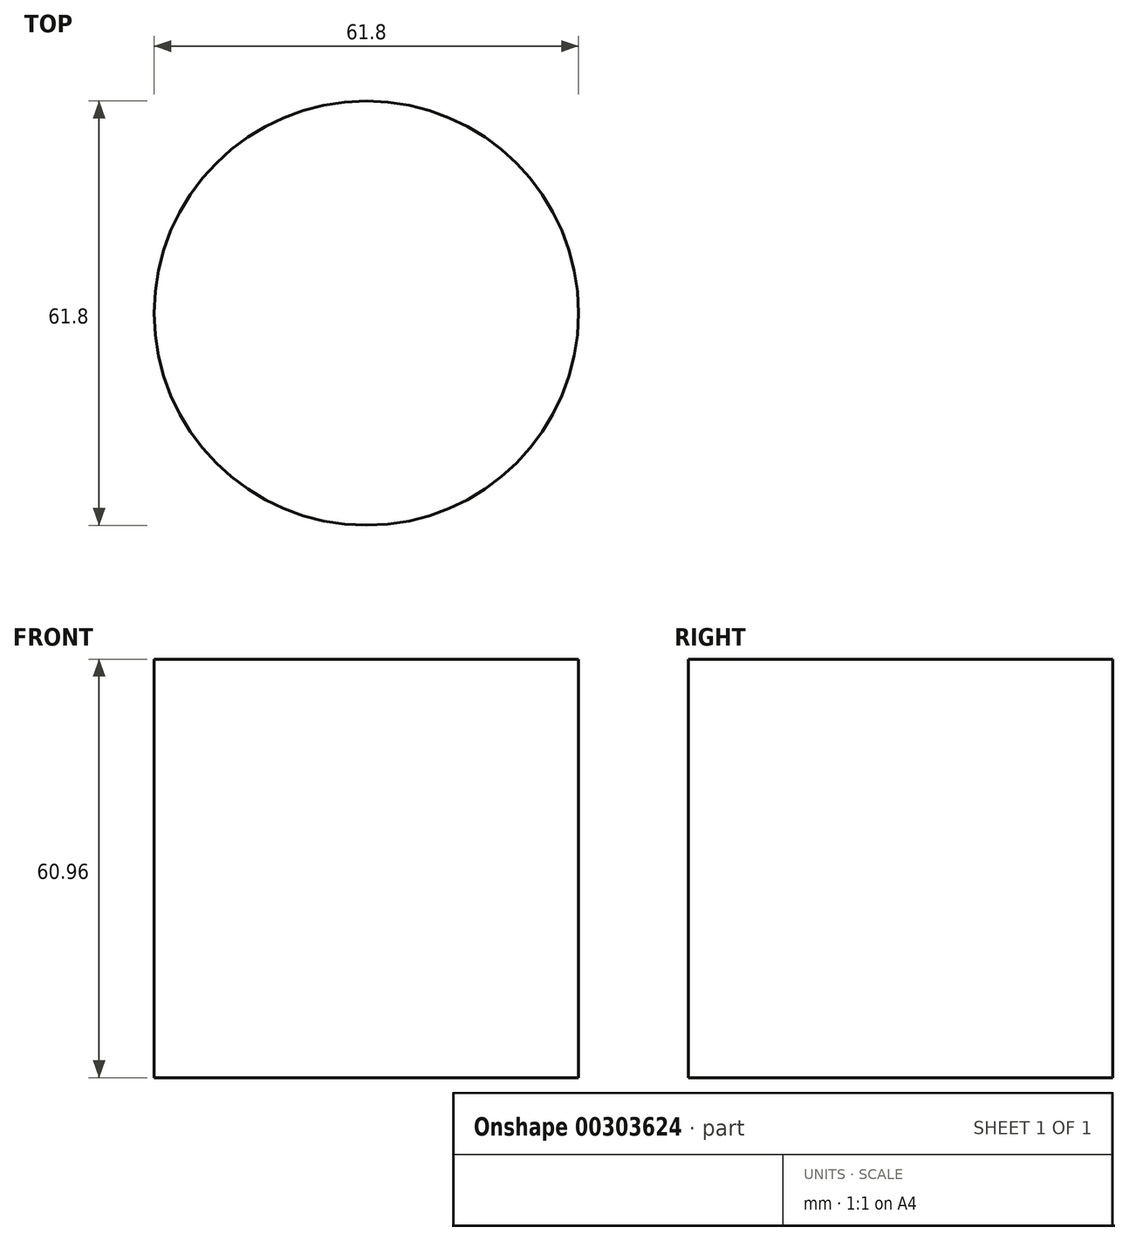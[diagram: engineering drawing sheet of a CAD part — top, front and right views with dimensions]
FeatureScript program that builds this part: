
annotation { "Feature Type Name" : "Feature", "Feature Type Description" : "" }
export const myFeature = defineFeature(function(context is Context, id is Id, definition is map)
    precondition{}
    {
        {
            var Q0;
            Q0=qCreatedBy(makeId("Top.planeOp"),FACE);
            var sketch = newSketch(context, id + "F0", { "sketchPlane" : qUnion([Q0])});
            skCircle(sketch, "E0", {"center": v(0, 0) * mm, "radius": 30.9 * mm});
            skSolve(sketch);
        }
        {
            var Q0;
            Q0=makeQuery(id+"F0.imprint","IMPRINT",FACE,{"disambiguationData":[TD([[makeQuery(id+"F0.imprint","IMPRINT",EDGE,{"derivedFrom":sQuery(id+"F0.wireOp",EDGE,"E0")}),1.0]])]});
            extrude(context, id + "F1", {"entities" : qUnion([Q0]), "depth" : 60.96 * mm});
        }
        {
            var Q0;
            Q0=qCreatedBy(makeId("Front.planeOp"),FACE);
            var sketch = newSketch(context, id + "F2", { "sketchPlane" : qUnion([Q0])});
            skLineSegment(sketch, "E1", {"start": v(0, 65.85) * mm, "end": v(-17.48, -29.67) * mm});
            skSolve(sketch);
        }
        {
            var Q0;
            Q0 = qSketchRegion(id + "F2", true);
            var Q1;
            Q1=sQuery(id+"F2.wireOp",EDGE,"E1");
            extrude(context, id + "F3", {"entities" : qUnion([Q0]), "bodyType" : ToolBodyType.SURFACE, "surfaceEntities" : qUnion([Q1]), "depth" : 47.5 * mm});
        }
    });
